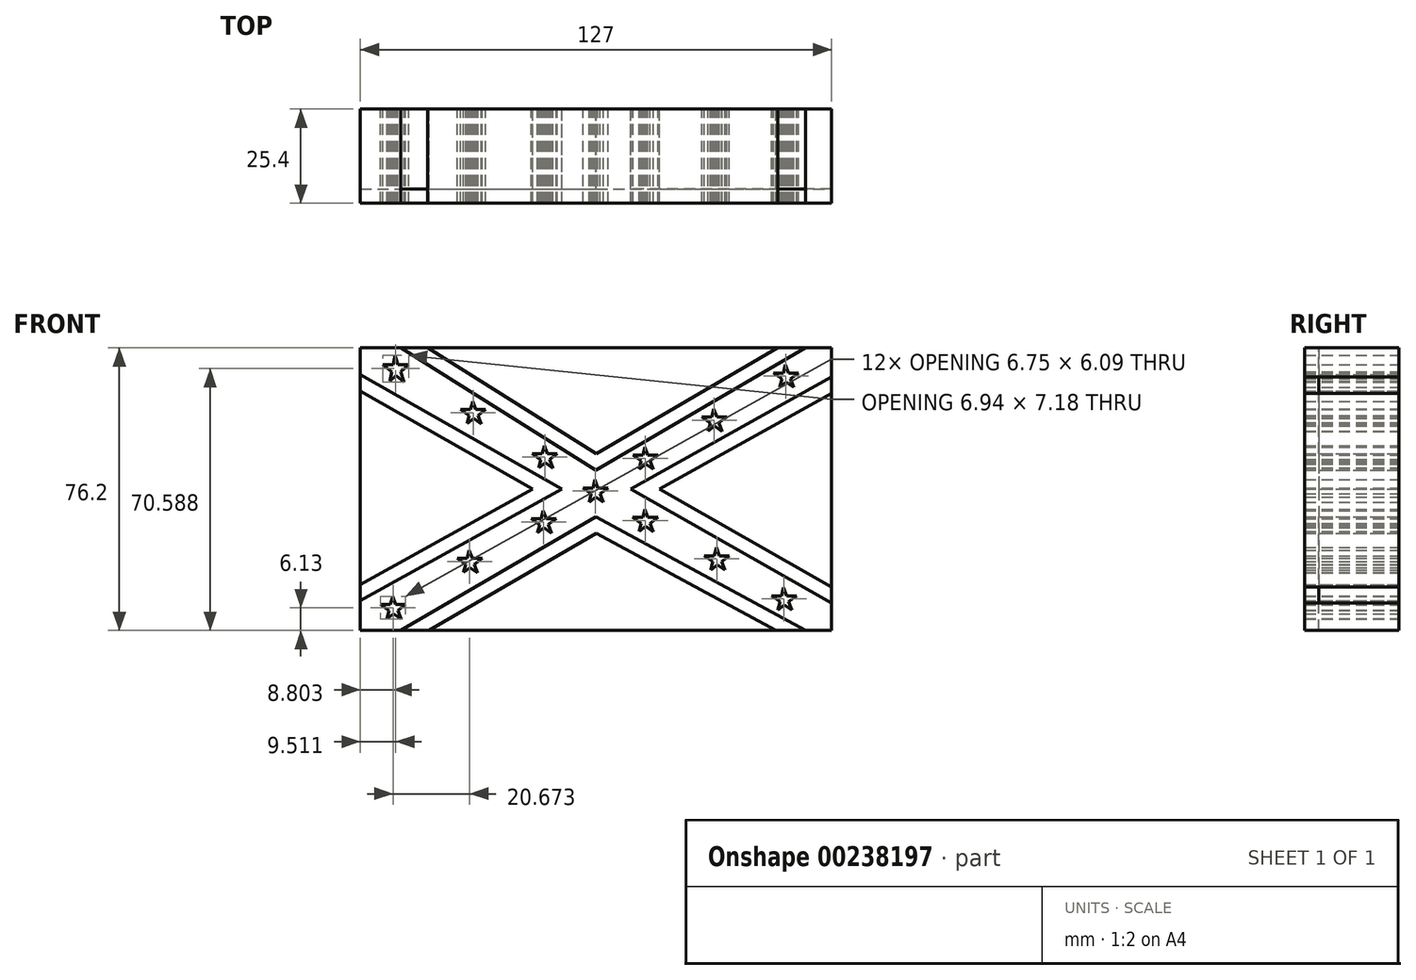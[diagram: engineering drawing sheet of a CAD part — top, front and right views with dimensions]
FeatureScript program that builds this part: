
annotation { "Feature Type Name" : "Feature", "Feature Type Description" : "" }
export const myFeature = defineFeature(function(context is Context, id is Id, definition is map)
    precondition{}
    {
        {
            var Q0;
            Q0=qCreatedBy(makeId("Front.planeOp"),FACE);
            var sketch = newSketch(context, id + "F0", { "sketchPlane" : qUnion([Q0])});
            skLineSegment(sketch, "E0.bottom", {"start": v(-45.23, 45.61) * mm, "end": v(81.77, 45.61) * mm});
            skLineSegment(sketch, "E0.top", {"start": v(-45.23, -30.59) * mm, "end": v(81.77, -30.59) * mm});
            skLineSegment(sketch, "E0.left", {"start": v(-45.23, 45.61) * mm, "end": v(-45.23, -30.59) * mm});
            skLineSegment(sketch, "E0.right", {"start": v(81.77, 45.61) * mm, "end": v(81.77, -30.59) * mm});
            skLineSegment(sketch, "E1", {"start": v(-34.32, 45.61) * mm, "end": v(18.27, 12.6) * mm});
            skLineSegment(sketch, "E2", {"start": v(18.27, 12.6) * mm, "end": v(74.8, 45.61) * mm});
            skLineSegment(sketch, "E3", {"start": v(-34.32, -30.59) * mm, "end": v(18.27, 0) * mm});
            skLineSegment(sketch, "E4", {"start": v(18.27, 0) * mm, "end": v(74.8, -30.59) * mm});
            skLineSegment(sketch, "E5", {"start": v(-45.23, 38.39) * mm, "end": v(9.05, 7.51) * mm});
            skLineSegment(sketch, "E6", {"start": v(9.05, 7.51) * mm, "end": v(-45.23, -22.57) * mm});
            skLineSegment(sketch, "E7", {"start": v(81.77, 37.7) * mm, "end": v(27.67, 7.51) * mm});
            skLineSegment(sketch, "E8", {"start": v(27.67, 7.51) * mm, "end": v(81.77, -23.26) * mm});
            skLineSegment(sketch, "E9", {"start": v(-39.2, 41.05) * mm, "end": v(-32.25, 41.05) * mm});
            skLineSegment(sketch, "E10", {"start": v(-32.25, 41.05) * mm, "end": v(-37.26, 36.65) * mm});
            skLineSegment(sketch, "E11", {"start": v(-37.26, 36.65) * mm, "end": v(-35.93, 43.59) * mm});
            skLineSegment(sketch, "E12", {"start": v(-35.93, 43.59) * mm, "end": v(-33.46, 36.4) * mm});
            skLineSegment(sketch, "E13", {"start": v(-33.46, 36.4) * mm, "end": v(-39.2, 41.05) * mm});
            skLineSegment(sketch, "E14", {"start": v(-18.21, 29) * mm, "end": v(-11.46, 29) * mm});
            skLineSegment(sketch, "E15", {"start": v(-11.46, 29) * mm, "end": v(-16.48, 25.2) * mm});
            skLineSegment(sketch, "E16", {"start": v(-16.48, 25.2) * mm, "end": v(-14.97, 31.2) * mm});
            skLineSegment(sketch, "E17", {"start": v(-14.97, 31.2) * mm, "end": v(-12.7, 25.1) * mm});
            skLineSegment(sketch, "E18", {"start": v(-12.7, 25.1) * mm, "end": v(-18.21, 29) * mm});
            skLineSegment(sketch, "E19", {"start": v(1.12, 17.08) * mm, "end": v(7.87, 17.08) * mm});
            skLineSegment(sketch, "E20", {"start": v(7.87, 17.08) * mm, "end": v(2.84, 13.28) * mm});
            skLineSegment(sketch, "E21", {"start": v(2.84, 13.28) * mm, "end": v(4.36, 19.27) * mm});
            skLineSegment(sketch, "E22", {"start": v(4.36, 19.27) * mm, "end": v(6.64, 13.19) * mm});
            skLineSegment(sketch, "E23", {"start": v(6.64, 13.19) * mm, "end": v(1.12, 17.08) * mm});
            skLineSegment(sketch, "E24", {"start": v(28.2, 16.7) * mm, "end": v(34.94, 16.7) * mm});
            skLineSegment(sketch, "E25", {"start": v(34.94, 16.7) * mm, "end": v(29.92, 12.9) * mm});
            skLineSegment(sketch, "E26", {"start": v(29.92, 12.9) * mm, "end": v(31.43, 18.9) * mm});
            skLineSegment(sketch, "E27", {"start": v(31.43, 18.9) * mm, "end": v(33.71, 12.81) * mm});
            skLineSegment(sketch, "E28", {"start": v(33.71, 12.81) * mm, "end": v(28.2, 16.7) * mm});
            skLineSegment(sketch, "E29", {"start": v(46.77, 26.98) * mm, "end": v(53.52, 26.98) * mm});
            skLineSegment(sketch, "E30", {"start": v(53.52, 26.98) * mm, "end": v(48.5, 23.17) * mm});
            skLineSegment(sketch, "E31", {"start": v(48.5, 23.17) * mm, "end": v(50, 29.17) * mm});
            skLineSegment(sketch, "E32", {"start": v(50, 29.17) * mm, "end": v(52.29, 23.09) * mm});
            skLineSegment(sketch, "E33", {"start": v(52.29, 23.09) * mm, "end": v(46.77, 26.98) * mm});
            skLineSegment(sketch, "E34", {"start": v(66.06, 38.82) * mm, "end": v(72.81, 38.82) * mm});
            skLineSegment(sketch, "E35", {"start": v(72.81, 38.82) * mm, "end": v(67.8, 35.01) * mm});
            skLineSegment(sketch, "E36", {"start": v(67.8, 35.01) * mm, "end": v(69.3, 41.01) * mm});
            skLineSegment(sketch, "E37", {"start": v(69.3, 41.01) * mm, "end": v(71.58, 34.93) * mm});
            skLineSegment(sketch, "E38", {"start": v(71.58, 34.93) * mm, "end": v(66.06, 38.82) * mm});
            skLineSegment(sketch, "E39", {"start": v(-39.8, -23.6) * mm, "end": v(-33.05, -23.6) * mm});
            skLineSegment(sketch, "E40", {"start": v(-33.05, -23.6) * mm, "end": v(-38.07, -27.42) * mm});
            skLineSegment(sketch, "E41", {"start": v(-38.07, -27.42) * mm, "end": v(-36.56, -21.42) * mm});
            skLineSegment(sketch, "E42", {"start": v(-36.56, -21.42) * mm, "end": v(-34.28, -27.5) * mm});
            skLineSegment(sketch, "E43", {"start": v(-34.28, -27.5) * mm, "end": v(-39.8, -23.6) * mm});
            skLineSegment(sketch, "E44", {"start": v(-19.13, -11.14) * mm, "end": v(-12.38, -11.14) * mm});
            skLineSegment(sketch, "E45", {"start": v(-12.38, -11.14) * mm, "end": v(-17.4, -14.95) * mm});
            skLineSegment(sketch, "E46", {"start": v(-17.4, -14.95) * mm, "end": v(-15.9, -8.95) * mm});
            skLineSegment(sketch, "E47", {"start": v(-15.9, -8.95) * mm, "end": v(-13.6, -15.04) * mm});
            skLineSegment(sketch, "E48", {"start": v(-13.6, -15.04) * mm, "end": v(-19.13, -11.14) * mm});
            skLineSegment(sketch, "E49", {"start": v(0.78, -0.46) * mm, "end": v(7.53, -0.46) * mm});
            skLineSegment(sketch, "E50", {"start": v(7.53, -0.46) * mm, "end": v(2.5, -4.26) * mm});
            skLineSegment(sketch, "E51", {"start": v(2.5, -4.26) * mm, "end": v(4.02, 1.73) * mm});
            skLineSegment(sketch, "E52", {"start": v(4.02, 1.73) * mm, "end": v(6.3, -4.35) * mm});
            skLineSegment(sketch, "E53", {"start": v(6.3, -4.35) * mm, "end": v(0.78, -0.46) * mm});
            skLineSegment(sketch, "E54", {"start": v(14.74, 7.85) * mm, "end": v(21.48, 7.85) * mm});
            skLineSegment(sketch, "E55", {"start": v(21.48, 7.85) * mm, "end": v(16.46, 4.04) * mm});
            skLineSegment(sketch, "E56", {"start": v(16.46, 4.04) * mm, "end": v(17.97, 10.04) * mm});
            skLineSegment(sketch, "E57", {"start": v(17.97, 10.04) * mm, "end": v(20.25, 3.96) * mm});
            skLineSegment(sketch, "E58", {"start": v(20.25, 3.96) * mm, "end": v(14.74, 7.85) * mm});
            skLineSegment(sketch, "E59.0", {"start": v(-32.3, 48.84) * mm, "end": v(20.3, 15.83) * mm});
            skLineSegment(sketch, "E60.0", {"start": v(16.35, 15.9) * mm, "end": v(72.87, 48.9) * mm});
            skLineSegment(sketch, "E61.0", {"start": v(83.63, 34.38) * mm, "end": v(29.52, 4.19) * mm});
            skLineSegment(sketch, "E62.0", {"start": v(29.55, 10.83) * mm, "end": v(83.65, -19.94) * mm});
            skLineSegment(sketch, "E63.0", {"start": v(18.34, -4.37) * mm, "end": v(72.98, -33.94) * mm});
            skLineSegment(sketch, "E63.1", {"start": v(-32.4, -33.88) * mm, "end": v(18.34, -4.37) * mm});
            skLineSegment(sketch, "E64.0", {"start": v(-47.11, 35.08) * mm, "end": v(7.17, 4.2) * mm});
            skLineSegment(sketch, "E65.0", {"start": v(7.2, 10.85) * mm, "end": v(-47.08, -19.24) * mm});
            skLineSegment(sketch, "E66", {"start": v(65.54, -21.24) * mm, "end": v(72.29, -21.24) * mm});
            skLineSegment(sketch, "E67", {"start": v(72.29, -21.24) * mm, "end": v(67.27, -25.04) * mm});
            skLineSegment(sketch, "E68", {"start": v(67.27, -25.04) * mm, "end": v(68.78, -19.05) * mm});
            skLineSegment(sketch, "E69", {"start": v(68.78, -19.05) * mm, "end": v(71.06, -25.13) * mm});
            skLineSegment(sketch, "E70", {"start": v(71.06, -25.13) * mm, "end": v(65.54, -21.24) * mm});
            skLineSegment(sketch, "E71", {"start": v(28.2, -0.09) * mm, "end": v(34.94, -0.09) * mm});
            skLineSegment(sketch, "E72", {"start": v(34.94, -0.09) * mm, "end": v(29.92, -3.9) * mm});
            skLineSegment(sketch, "E73", {"start": v(29.92, -3.9) * mm, "end": v(31.43, 2.1) * mm});
            skLineSegment(sketch, "E74", {"start": v(31.43, 2.1) * mm, "end": v(33.7, -3.98) * mm});
            skLineSegment(sketch, "E75", {"start": v(33.7, -3.98) * mm, "end": v(28.2, -0.09) * mm});
            skLineSegment(sketch, "E76", {"start": v(47.45, -10.46) * mm, "end": v(54.2, -10.46) * mm});
            skLineSegment(sketch, "E77", {"start": v(54.2, -10.46) * mm, "end": v(49.17, -14.27) * mm});
            skLineSegment(sketch, "E78", {"start": v(49.17, -14.27) * mm, "end": v(50.68, -8.27) * mm});
            skLineSegment(sketch, "E79", {"start": v(50.68, -8.27) * mm, "end": v(52.96, -14.36) * mm});
            skLineSegment(sketch, "E80", {"start": v(52.96, -14.36) * mm, "end": v(47.45, -10.46) * mm});
            skSolve(sketch);
        }
        {
            var Q0;
            {var subQ0=sQuery(id+"F0.wireOp",EDGE,"E59.0");var subQ1=sQuery(id+"F0.wireOp",EDGE,"E0.bottom");var subQ2=makeQuery(id+"F0.imprint","INTERSECT",VERTEX,{"derivedFrom":[subQ1,subQ0]});Q0=makeQuery(id+"F0.imprint","IMPRINT",FACE,{"disambiguationData":[TD([[makeQuery(id+"F0.imprint","IMPRINT",EDGE,{"disambiguationData":[TD([[subQ2,-1.0]])],"derivedFrom":subQ1}),-1.0]])]});}
            var Q1;
            {var subQ0=sQuery(id+"F0.wireOp",EDGE,"E64.0");var subQ1=sQuery(id+"F0.wireOp",EDGE,"E0.left");var subQ2=makeQuery(id+"F0.imprint","INTERSECT",VERTEX,{"derivedFrom":[subQ1,subQ0]});Q1=makeQuery(id+"F0.imprint","IMPRINT",FACE,{"disambiguationData":[TD([[makeQuery(id+"F0.imprint","IMPRINT",EDGE,{"disambiguationData":[TD([[subQ2,-1.0]])],"derivedFrom":subQ1}),1.0]])]});}
            var Q2;
            {var subQ0=sQuery(id+"F0.wireOp",EDGE,"E63.1");var subQ1=sQuery(id+"F0.wireOp",EDGE,"E0.top");var subQ2=makeQuery(id+"F0.imprint","INTERSECT",VERTEX,{"derivedFrom":[subQ1,subQ0]});Q2=makeQuery(id+"F0.imprint","IMPRINT",FACE,{"disambiguationData":[TD([[makeQuery(id+"F0.imprint","IMPRINT",EDGE,{"disambiguationData":[TD([[subQ2,-1.0]])],"derivedFrom":subQ1}),1.0]])]});}
            var Q3;
            {var subQ0=sQuery(id+"F0.wireOp",EDGE,"E61.0");var subQ1=sQuery(id+"F0.wireOp",EDGE,"E0.right");var subQ2=makeQuery(id+"F0.imprint","INTERSECT",VERTEX,{"derivedFrom":[subQ1,subQ0]});Q3=makeQuery(id+"F0.imprint","IMPRINT",FACE,{"disambiguationData":[TD([[makeQuery(id+"F0.imprint","IMPRINT",EDGE,{"disambiguationData":[TD([[subQ2,-1.0]])],"derivedFrom":subQ1}),-1.0]])]});}
            var Q4;
            {var subQ167=sQuery(id+"F0.wireOp",EDGE,"E1");Q4=makeQuery(id+"F0.imprint","IMPRINT",FACE,{"disambiguationData":[TD([[makeQuery(id+"F0.imprint","IMPRINT",EDGE,{"derivedFrom":subQ167}),-1.0]])]});}
            extrude(context, id + "F1", {"entities" : qUnion([Q0, Q1, Q2, Q3, Q4]), "depth" : 25.4 * mm});
        }
        {
            var Q0;
            {var subQ1=sQuery(id+"F0.wireOp",EDGE,"E1");Q0=makeQuery(id+"F0.imprint","IMPRINT",FACE,{"disambiguationData":[TD([[makeQuery(id+"F0.imprint","IMPRINT",EDGE,{"derivedFrom":subQ1}),1.0]])]});}
            var Q1;
            {var subQ0=sQuery(id+"F0.wireOp",EDGE,"E5");var subQ1=sQuery(id+"F0.wireOp",EDGE,"E0.left");var subQ2=makeQuery(id+"F0.imprint","INTERSECT",VERTEX,{"derivedFrom":[subQ1,subQ0]});Q1=makeQuery(id+"F0.imprint","IMPRINT",FACE,{"disambiguationData":[TD([[makeQuery(id+"F0.imprint","IMPRINT",EDGE,{"disambiguationData":[TD([[subQ2,-1.0]])],"derivedFrom":subQ1}),1.0]])]});}
            var Q2;
            {var subQ1=sQuery(id+"F0.wireOp",EDGE,"E3");Q2=makeQuery(id+"F0.imprint","IMPRINT",FACE,{"disambiguationData":[TD([[makeQuery(id+"F0.imprint","IMPRINT",EDGE,{"derivedFrom":subQ1}),-1.0]])]});}
            var Q3;
            {var subQ0=sQuery(id+"F0.wireOp",EDGE,"E8");var subQ1=sQuery(id+"F0.wireOp",EDGE,"E0.right");var subQ2=makeQuery(id+"F0.imprint","INTERSECT",VERTEX,{"derivedFrom":[subQ1,subQ0]});Q3=makeQuery(id+"F0.imprint","IMPRINT",FACE,{"disambiguationData":[TD([[makeQuery(id+"F0.imprint","IMPRINT",EDGE,{"disambiguationData":[TD([[subQ2,1.0]])],"derivedFrom":subQ1}),-1.0]])]});}
            var Q4;
            {var subQ0=sQuery(id+"F0.wireOp",EDGE,"E7");var subQ1=sQuery(id+"F0.wireOp",EDGE,"E0.right");var subQ2=makeQuery(id+"F0.imprint","INTERSECT",VERTEX,{"derivedFrom":[subQ1,subQ0]});Q4=makeQuery(id+"F0.imprint","IMPRINT",FACE,{"disambiguationData":[TD([[makeQuery(id+"F0.imprint","IMPRINT",EDGE,{"disambiguationData":[TD([[subQ2,-1.0]])],"derivedFrom":subQ1}),-1.0]])]});}
            var Q5;
            {var subQ0=sQuery(id+"F0.wireOp",EDGE,"E8");var subQ1=sQuery(id+"F0.wireOp",EDGE,"E7");var subQ2=makeQuery(id+"F0.imprint","INTERSECT",VERTEX,{"derivedFrom":[subQ1,subQ0]});Q5=makeQuery(id+"F0.imprint","IMPRINT",FACE,{"disambiguationData":[TD([[makeQuery(id+"F0.imprint","IMPRINT",EDGE,{"disambiguationData":[TD([[subQ2,1.0]])],"derivedFrom":subQ1}),1.0]])]});}
            var Q6;
            {var subQ0=sQuery(id+"F0.wireOp",EDGE,"E6");var subQ1=sQuery(id+"F0.wireOp",EDGE,"E0.left");var subQ2=makeQuery(id+"F0.imprint","INTERSECT",VERTEX,{"derivedFrom":[subQ1,subQ0]});Q6=makeQuery(id+"F0.imprint","IMPRINT",FACE,{"disambiguationData":[TD([[makeQuery(id+"F0.imprint","IMPRINT",EDGE,{"disambiguationData":[TD([[subQ2,1.0]])],"derivedFrom":subQ1}),1.0]])]});}
            var Q7;
            {var subQ0=sQuery(id+"F0.wireOp",EDGE,"E6");var subQ1=sQuery(id+"F0.wireOp",EDGE,"E5");var subQ2=makeQuery(id+"F0.imprint","INTERSECT",VERTEX,{"derivedFrom":[subQ1,subQ0]});Q7=makeQuery(id+"F0.imprint","IMPRINT",FACE,{"disambiguationData":[TD([[makeQuery(id+"F0.imprint","IMPRINT",EDGE,{"disambiguationData":[TD([[subQ2,1.0]])],"derivedFrom":subQ1}),-1.0]])]});}
            extrude(context, id + "F2", {"entities" : qUnion([Q0, Q1, Q2, Q3, Q4, Q5, Q6, Q7]), "depth" : 21.59 * mm});
        }
    });
